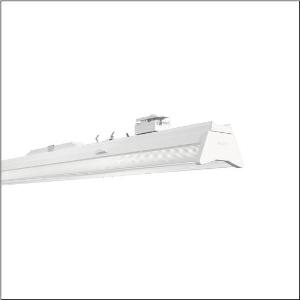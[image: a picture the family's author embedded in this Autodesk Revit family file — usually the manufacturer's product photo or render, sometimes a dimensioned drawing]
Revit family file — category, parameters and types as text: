
# Revit family: licross_r__21_performance_mo_52tm167n445g_e37c
name_source: partatom
category: Lighting Fixtures
units: mm (PartAtom-declared; Revit-internal decimal feet)

## family parameters
Cut with Voids When Loaded = No
Host = Face
Light Source = No
Part Type = Normal
Room Calculation Point = No
Round Connector Dimension = Use Diameter
Shared = No

## types (1)
- Licross® 21 Performance MO (1 x LED, 4580 lm, 24.7 W, 4000K)
    Apparent Load = 25 VA
    CIE Flux Codes = 66 88 96 79 100
    Color Rendering = 80
    Color Temperature = 4000K
    Default Elevation = 1800 mm
    Description = Licross® 21 Performance MO, luminaire insert, of sheet steel, galvanised, coil coated, white, length: 1.500mm, width: 120mm, height: 123mm, LED rated luminous flux: 4.580lm, light colour: 840, SDCM (Standard Deviation of Colour Matching)MacAdam ≤ 3 SDCM (initial), control gear: ON/OFF, with plug, 3-pole, with phase selection, mains connection: 220..240V, AC, 50/60Hz, rated input power: 25W, internal wiring halogen-free, primary light control with lens, of plastic, primary optical cover: cover, of PMMA, CAT 2 (L<= 3000cd/m²), light emission: direct/indirect distribution, primary light characteristic: symmetric, protection rating (complete): IP40, insulation class (complete): insulation class I (protective earthing), certification: CE, ENEC, UKCA, protection symbol: D if used in an environment without relevant dust loads with corresponding accessories, impact resistance: IK06, permissible ambient temperature for indoor applications: -35..+55°C, corresponds to IFS (International Featured Standards) requirements for safety and quality in the food industry, reducing of maximum allowable ambient temperature of 5°C with ceiling mounting, LABS conformity tested according to VDMA 24364:2018-05, packaging unit: 1 piece
    Height = 114 mm
    Lamp = 1 x LED
    Lamp Light Flux = 4580 lm
    Lamp Power = 24.7 W
    Lamp count = 1
    Length = 1500 mm
    Luminous efficacy = 185 lm/W
    Manufacturer = Siteco
    ModVariant = No
    Model = 52TM167N445G
    Mounting Place = Ceiling
    Mounting Type = Pendant
    Number of Poles = 1
    OnlyDefault = Yes
    Power Factor = 1
    Product Name = Licross® 21 Performance MO
    Product group = luminaire insert | ceiling pendant
    ProductGroupID = 901
    Protection Class = Protection class I
    Protection Degree = IP 40
    RLX_Detail_Level = 1
    RLX_Emergency_Light_Flux = 0 lm
    RLX_Emergency_Type = 0
    RLX_Emergency_Type_DB = No
    RlxData = <blob elided: 30601 chars, md5=6878f0c2>
    Socket = socket
    Standby Power = 0 W
    System Light Flux = 4580 lm
    System Power = 25 W
    Type Comments = Product without accessories
    Type Image = l_1256138.jpg
    URL = http://relux.com
    VarID = ---
    Voltage = 0 V
    Weight = 0.00 kg
    Width = 120 mm

## geometry (parser evidence)
native form markers: Blend x4, Sweep x13
no freeform markers — native parametric forms only
